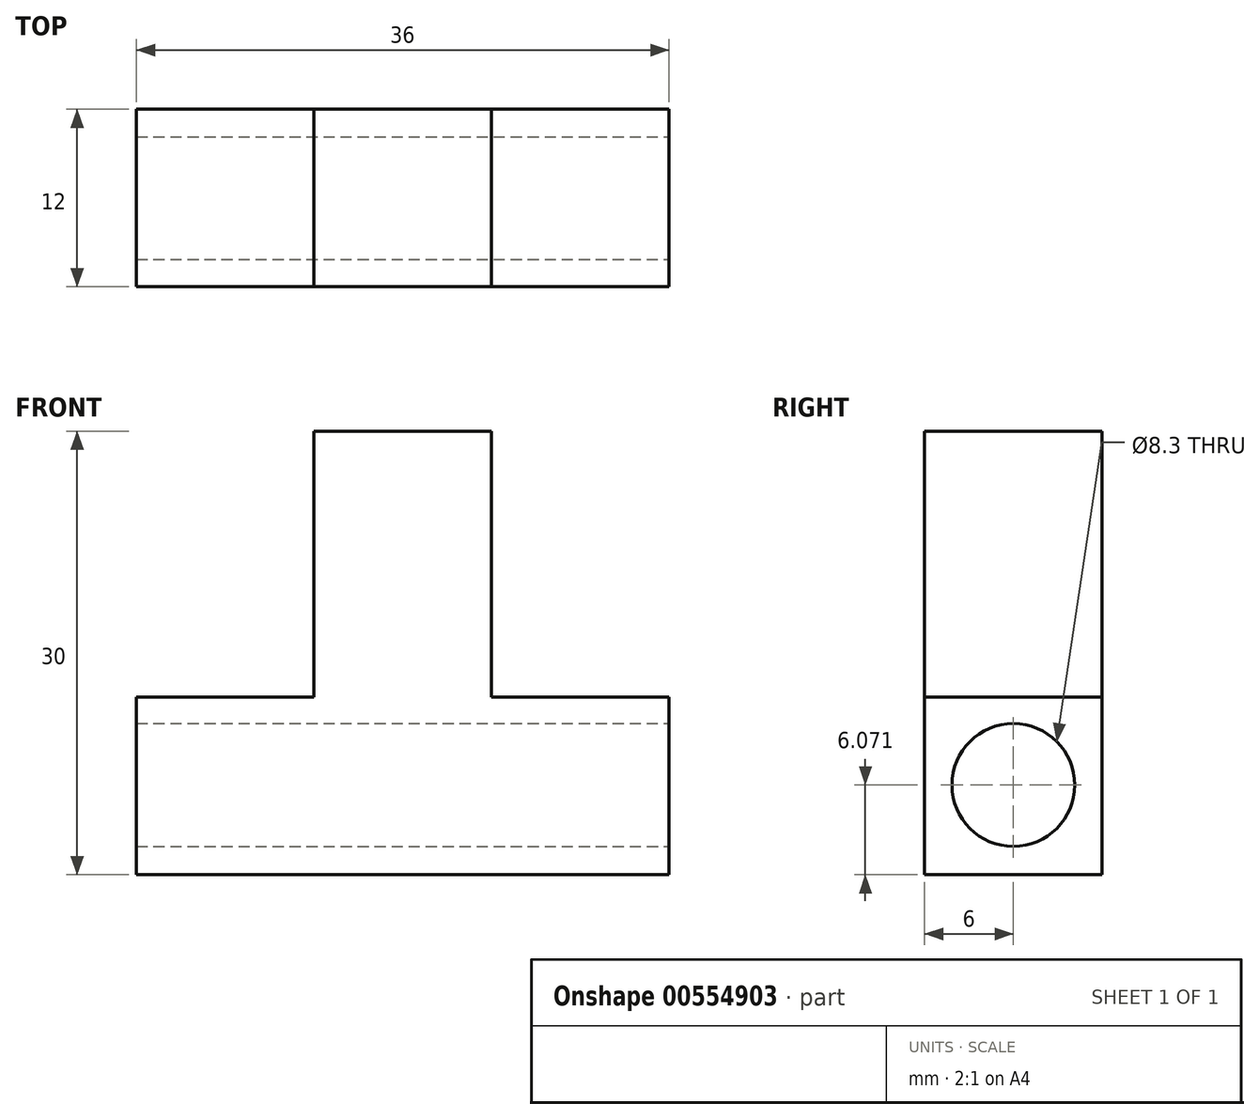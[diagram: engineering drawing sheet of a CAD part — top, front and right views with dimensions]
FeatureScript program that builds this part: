
annotation { "Feature Type Name" : "Feature", "Feature Type Description" : "" }
export const myFeature = defineFeature(function(context is Context, id is Id, definition is map)
    precondition{}
    {
        {
            var Q0;
            Q0=qCreatedBy(makeId("Top.planeOp"),FACE);
            var sketch = newSketch(context, id + "F0", { "sketchPlane" : qUnion([Q0])});
            skLineSegment(sketch, "E0.bottom", {"start": v(6, -6) * mm, "end": v(-6, -6) * mm});
            skLineSegment(sketch, "E0.top", {"start": v(6, 6) * mm, "end": v(-6, 6) * mm});
            skLineSegment(sketch, "E0.left", {"start": v(6, -6) * mm, "end": v(6, 6) * mm});
            skLineSegment(sketch, "E0.right", {"start": v(-6, -6) * mm, "end": v(-6, 6) * mm});
            skPoint(sketch, "E0.middle", {"position": v(0, 0) * mm});
            skLineSegment(sketch, "E1.bottom", {"start": v(-6, 6) * mm, "end": v(-18, 6) * mm});
            skLineSegment(sketch, "E1.top", {"start": v(-6, -6) * mm, "end": v(-18, -6) * mm});
            skLineSegment(sketch, "E1.left", {"start": v(-6, 6) * mm, "end": v(-6, -6) * mm});
            skLineSegment(sketch, "E1.right", {"start": v(-18, 6) * mm, "end": v(-18, -6) * mm});
            skLineSegment(sketch, "E2.bottom", {"start": v(6, 6) * mm, "end": v(18, 6) * mm});
            skLineSegment(sketch, "E2.top", {"start": v(6, -6) * mm, "end": v(18, -6) * mm});
            skLineSegment(sketch, "E2.left", {"start": v(6, 6) * mm, "end": v(6, -6) * mm});
            skLineSegment(sketch, "E2.right", {"start": v(18, 6) * mm, "end": v(18, -6) * mm});
            skSolve(sketch);
        }
        {
            var Q0;
            Q0=makeQuery(id+"F0.imprint","IMPRINT",FACE,{"disambiguationData":[TD([[makeQuery(id+"F0.imprint","IMPRINT",EDGE,{"derivedFrom":sQuery(id+"F0.wireOp",EDGE,"E0.bottom")}),-1.0]])]});
            extrude(context, id + "F1", {"entities" : qUnion([Q0]), "depth" : 30 * mm, "offsetDistance" : 25 * mm});
        }
        {
            var Q0;
            Q0=makeQuery(id+"F0.imprint","IMPRINT",FACE,{"disambiguationData":[TD([[makeQuery(id+"F0.imprint","IMPRINT",EDGE,{"derivedFrom":sQuery(id+"F0.wireOp",EDGE,"E1.bottom")}),1.0]])]});
            var Q1;
            Q1=makeQuery(id+"F0.imprint","IMPRINT",FACE,{"disambiguationData":[TD([[makeQuery(id+"F0.imprint","IMPRINT",EDGE,{"derivedFrom":sQuery(id+"F0.wireOp",EDGE,"E2.bottom")}),-1.0]])]});
            extrude(context, id + "F2", {"entities" : qUnion([Q0, Q1]), "operationType" : NewBodyOperationType.ADD, "depth" : 12 * mm, "offsetDistance" : 25 * mm});
        }
        {
            var Q0;
            Q0=makeQuery(id+"F2.opExtrude","SWEPT_FACE",FACE,{"disambiguationData":[OSD([sQuery(id+"F0.wireOp",EDGE,"E2.right")])]});
            var sketch = newSketch(context, id + "F3", { "sketchPlane" : qUnion([Q0])});
            skCircle(sketch, "E3", {"center": v(0, 6.07) * mm, "radius": 4.15 * mm});
            skPoint(sketch, "E3.centerSnap0", {"position": v(0, 0) * mm});
            skSolve(sketch);
        }
        {
            var Q0;
            Q0=makeQuery(id+"F3.imprint","IMPRINT",FACE,{"disambiguationData":[TD([[makeQuery(id+"F3.imprint","IMPRINT",EDGE,{"derivedFrom":sQuery(id+"F3.wireOp",EDGE,"E3")}),1.0]])]});
            extrude(context, id + "F4", {"entities" : qUnion([Q0]), "operationType" : NewBodyOperationType.REMOVE, "oppositeDirection" : true, "depth" : 45 * mm, "offsetDistance" : 25 * mm});
        }
    });
